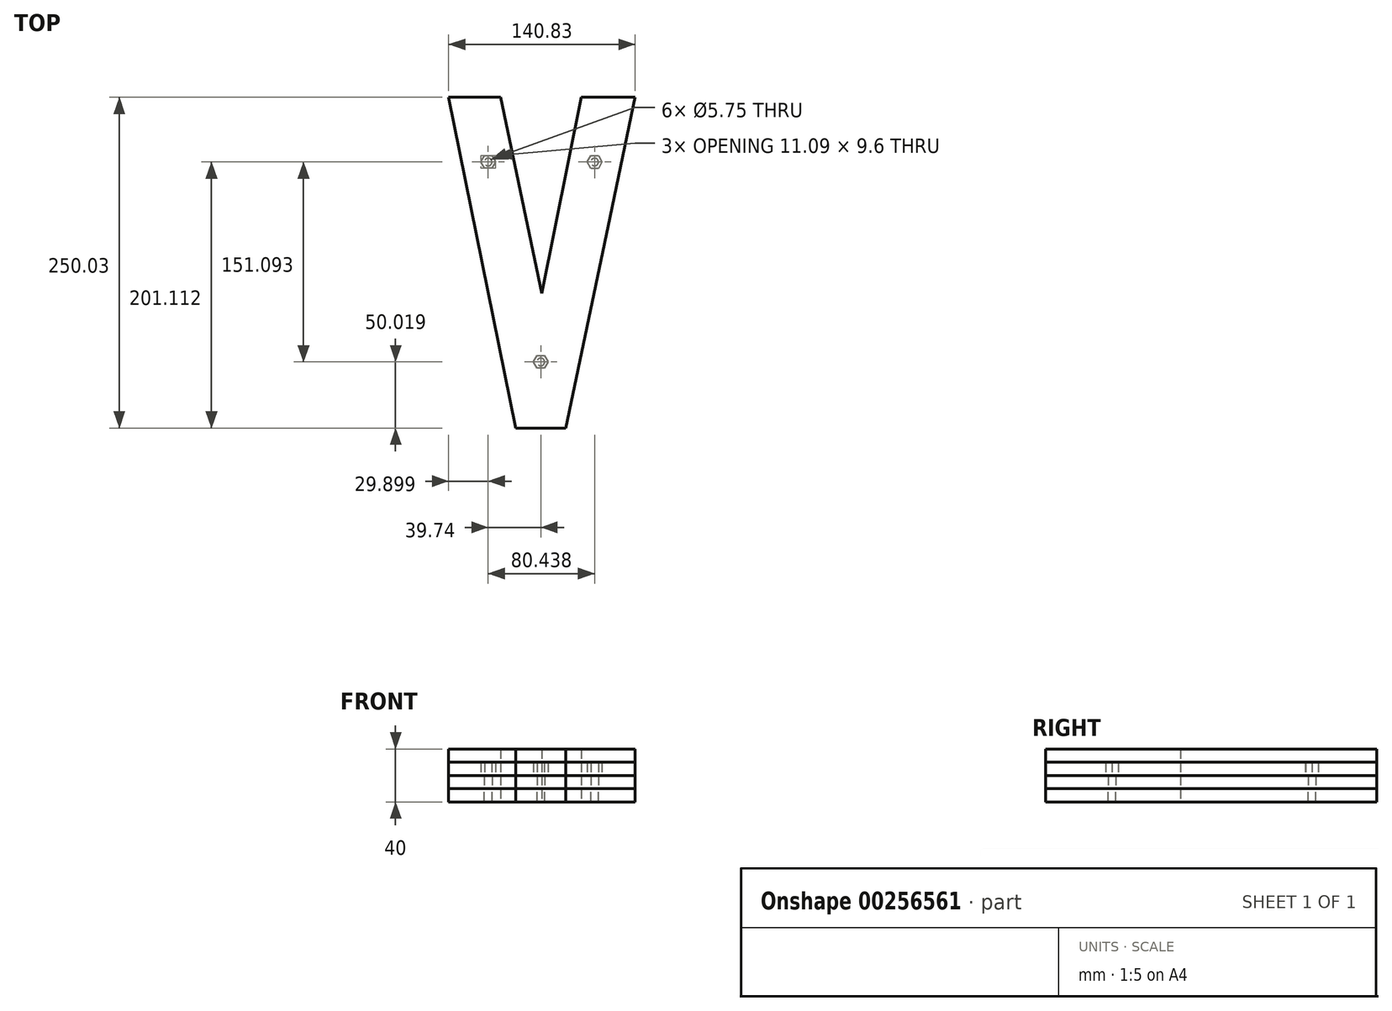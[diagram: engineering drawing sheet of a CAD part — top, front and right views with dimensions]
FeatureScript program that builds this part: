
annotation { "Feature Type Name" : "Feature", "Feature Type Description" : "" }
export const myFeature = defineFeature(function(context is Context, id is Id, definition is map)
    precondition{}
    {
        {
            assignVariable(context, id + "F0", {"name" : "spessore_materiale", "anyValue" : 10 * mm});
        }
        {
            var Q0;
            Q0=qCreatedBy(makeId("Top.planeOp"),FACE);
            var sketch = newSketch(context, id + "F1", { "sketchPlane" : qUnion([Q0])});
            skLineSegment(sketch, "E0", {"start": v(35.05, -81.42) * mm, "end": v(-32.7, -81.42) * mm});
            skLineSegment(sketch, "E1", {"start": v(-32.7, -81.42) * mm, "end": v(-112.73, 81.45) * mm});
            skLineSegment(sketch, "E2", {"start": v(-112.73, 81.45) * mm, "end": v(-56.97, 81.45) * mm});
            skLineSegment(sketch, "E3", {"start": v(-56.97, 81.45) * mm, "end": v(-0.74, -33) * mm});
            skLineSegment(sketch, "E4", {"start": v(-0.74, -33) * mm, "end": v(100.6, 204.64) * mm});
            skLineSegment(sketch, "E5", {"start": v(100.6, 204.64) * mm, "end": v(109.53, 225.59) * mm});
            skFitSpline(sketch, "E6", {"points": [v(109.53, 225.59) * mm, v(101.4, 226.06) * mm, v(93.16, 226.36) * mm, v(84.86, 226.36) * mm]});
            skFitSpline(sketch, "E7", {"points": [v(84.86, 226.36) * mm, v(83.84, 226.36) * mm, v(82.9, 226.32) * mm, v(81.9, 226.3) * mm]});
            skFitSpline(sketch, "E8", {"points": [v(81.9, 226.3) * mm, v(-87.62, 225.12) * mm, v(-225.03, 124.1) * mm, v(-225.03, 0) * mm]});
            skFitSpline(sketch, "E9", {"points": [v(-225.03, 0) * mm, v(-225.03, -111.84) * mm, v(-113.38, -204.88) * mm, v(32.74, -223.05) * mm]});
            skLineSegment(sketch, "E10", {"start": v(32.74, -223.05) * mm, "end": v(41.46, -202.6) * mm});
            skFitSpline(sketch, "E11", {"points": [v(41.46, -202.6) * mm, v(-97.09, -187.68) * mm, v(-203.61, -102.5) * mm, v(-203.61, 0) * mm]});
            skFitSpline(sketch, "E12", {"points": [v(-203.61, 0) * mm, v(-203.61, 110.11) * mm, v(-80.73, 200.17) * mm, v(72.69, 204.72) * mm]});
            skLineSegment(sketch, "E13", {"start": v(72.69, 204.72) * mm, "end": v(-2.4, 28.63) * mm});
            skLineSegment(sketch, "E14", {"start": v(-2.4, 28.63) * mm, "end": v(-40.98, 107.15) * mm});
            skLineSegment(sketch, "E15", {"start": v(-40.98, 107.15) * mm, "end": v(-153.98, 107.15) * mm});
            skLineSegment(sketch, "E16", {"start": v(-153.98, 107.15) * mm, "end": v(-54.89, -94.58) * mm});
            skLineSegment(sketch, "E17", {"start": v(-54.89, -94.58) * mm, "end": v(-60.1, -107.14) * mm});
            skLineSegment(sketch, "E18", {"start": v(-60.1, -107.14) * mm, "end": v(43.68, -107.14) * mm});
            skLineSegment(sketch, "E19", {"start": v(43.68, -107.14) * mm, "end": v(54.3, -107.06) * mm});
            skLineSegment(sketch, "E20", {"start": v(54.3, -107.06) * mm, "end": v(59, -96.15) * mm});
            skLineSegment(sketch, "E21", {"start": v(59, -96.15) * mm, "end": v(98.52, -3.43) * mm});
            skLineSegment(sketch, "E22", {"start": v(98.52, -3.43) * mm, "end": v(68.3, -3.43) * mm});
            skLineSegment(sketch, "E23", {"start": v(68.3, -3.43) * mm, "end": v(35.05, -81.42) * mm});
            skLineSegment(sketch, "E24", {"start": v(137.86, 222.98) * mm, "end": v(129.12, 202.52) * mm});
            skFitSpline(sketch, "E25", {"points": [v(129.12, 202.52) * mm, v(267.28, 187.34) * mm, v(373.37, 102.32) * mm, v(373.37, 0) * mm]});
            skFitSpline(sketch, "E26", {"points": [v(373.37, 0) * mm, v(373.37, -110.1) * mm, v(250.5, -200.17) * mm, v(97.07, -204.72) * mm]});
            skLineSegment(sketch, "E27", {"start": v(97.07, -204.72) * mm, "end": v(172.15, -28.63) * mm});
            skLineSegment(sketch, "E28", {"start": v(172.15, -28.63) * mm, "end": v(210.78, -107.14) * mm});
            skLineSegment(sketch, "E29", {"start": v(210.78, -107.14) * mm, "end": v(323.78, -107.14) * mm});
            skLineSegment(sketch, "E30", {"start": v(323.78, -107.14) * mm, "end": v(224.66, 94.57) * mm});
            skLineSegment(sketch, "E31", {"start": v(224.66, 94.57) * mm, "end": v(229.86, 107.15) * mm});
            skLineSegment(sketch, "E32", {"start": v(229.86, 107.15) * mm, "end": v(126.1, 107.15) * mm});
            skLineSegment(sketch, "E33", {"start": v(126.1, 107.15) * mm, "end": v(115.42, 107.07) * mm});
            skLineSegment(sketch, "E34", {"start": v(115.42, 107.07) * mm, "end": v(110.77, 96.15) * mm});
            skLineSegment(sketch, "E35", {"start": v(110.77, 96.15) * mm, "end": v(68.3, -3.43) * mm});
            skLineSegment(sketch, "E36", {"start": v(68.3, -3.43) * mm, "end": v(98.52, -3.43) * mm});
            skLineSegment(sketch, "E37", {"start": v(98.52, -3.43) * mm, "end": v(134.69, 81.45) * mm});
            skLineSegment(sketch, "E38", {"start": v(134.69, 81.45) * mm, "end": v(202.47, 81.45) * mm});
            skLineSegment(sketch, "E39", {"start": v(202.47, 81.45) * mm, "end": v(282.51, -81.42) * mm});
            skLineSegment(sketch, "E40", {"start": v(282.51, -81.42) * mm, "end": v(226.76, -81.42) * mm});
            skLineSegment(sketch, "E41", {"start": v(226.76, -81.42) * mm, "end": v(170.53, 33) * mm});
            skLineSegment(sketch, "E42", {"start": v(170.53, 33) * mm, "end": v(69.16, -204.63) * mm});
            skLineSegment(sketch, "E43", {"start": v(69.16, -204.63) * mm, "end": v(60.26, -225.59) * mm});
            skFitSpline(sketch, "E44", {"points": [v(60.26, -225.59) * mm, v(68.36, -226.07) * mm, v(76.57, -226.36) * mm, v(84.86, -226.36) * mm]});
            skFitSpline(sketch, "E45", {"points": [v(84.86, -226.36) * mm, v(85.9, -226.36) * mm, v(86.86, -226.32) * mm, v(87.87, -226.32) * mm]});
            skFitSpline(sketch, "E46", {"points": [v(87.87, -226.32) * mm, v(257.36, -225.13) * mm, v(394.8, -124.08) * mm, v(394.8, 0) * mm]});
            skFitSpline(sketch, "E47", {"points": [v(394.8, 0) * mm, v(394.8, 111.62) * mm, v(283.58, 204.54) * mm, v(137.86, 222.98) * mm]});
            skFitSpline(sketch, "E48", {"points": [v(-624, 127.8) * mm, v(-635.1, 127.8) * mm, v(-645.9, 124.08) * mm, v(-654.8, 117.24) * mm]});
            skFitSpline(sketch, "E49", {"points": [v(-654.8, 117.24) * mm, v(-663.7, 124.08) * mm, v(-674.5, 127.8) * mm, v(-685.62, 127.8) * mm]});
            skFitSpline(sketch, "E50", {"points": [v(-685.62, 127.8) * mm, v(-713.74, 127.8) * mm, v(-736.62, 104.92) * mm, v(-736.62, 76.78) * mm]});
            skLineSegment(sketch, "E51", {"start": v(-736.62, 76.78) * mm, "end": v(-736.62, -123.73) * mm});
            skLineSegment(sketch, "E52", {"start": v(-736.62, -123.73) * mm, "end": v(-696.19, -123.73) * mm});
            skLineSegment(sketch, "E53", {"start": v(-696.19, -123.73) * mm, "end": v(-696.19, 76.78) * mm});
            skFitSpline(sketch, "E54", {"points": [v(-696.19, 76.78) * mm, v(-696.19, 82.6) * mm, v(-691.43, 87.35) * mm, v(-685.62, 87.35) * mm]});
            skFitSpline(sketch, "E55", {"points": [v(-685.62, 87.35) * mm, v(-679.76, 87.35) * mm, v(-675.03, 82.6) * mm, v(-675.03, 76.78) * mm]});
            skLineSegment(sketch, "E56", {"start": v(-675.03, 76.78) * mm, "end": v(-675.03, -123.73) * mm});
            skLineSegment(sketch, "E57", {"start": v(-675.03, -123.73) * mm, "end": v(-634.58, -123.73) * mm});
            skLineSegment(sketch, "E58", {"start": v(-634.58, -123.73) * mm, "end": v(-634.58, 76.78) * mm});
            skFitSpline(sketch, "E59", {"points": [v(-634.58, 76.78) * mm, v(-634.58, 82.6) * mm, v(-629.83, 87.35) * mm, v(-624, 87.35) * mm]});
            skFitSpline(sketch, "E60", {"points": [v(-624, 87.35) * mm, v(-618.16, 87.35) * mm, v(-613.4, 82.6) * mm, v(-613.4, 76.78) * mm]});
            skLineSegment(sketch, "E61", {"start": v(-613.4, 76.78) * mm, "end": v(-613.4, -123.73) * mm});
            skLineSegment(sketch, "E62", {"start": v(-613.4, -123.73) * mm, "end": v(-572.97, -123.73) * mm});
            skLineSegment(sketch, "E63", {"start": v(-572.97, -123.73) * mm, "end": v(-572.97, 76.78) * mm});
            skFitSpline(sketch, "E64", {"points": [v(-572.97, 76.78) * mm, v(-572.97, 104.92) * mm, v(-595.85, 127.8) * mm, v(-624, 127.8) * mm]});
            skLineSegment(sketch, "E65", {"start": v(-331.84, -21.2) * mm, "end": v(-364.08, -21.2) * mm});
            skLineSegment(sketch, "E66", {"start": v(-364.08, -21.2) * mm, "end": v(-364.08, 69.71) * mm});
            skFitSpline(sketch, "E67", {"points": [v(-364.08, 69.71) * mm, v(-364.08, 78.61) * mm, v(-356.86, 85.84) * mm, v(-347.97, 85.84) * mm]});
            skFitSpline(sketch, "E68", {"points": [v(-347.97, 85.84) * mm, v(-339.08, 85.84) * mm, v(-331.84, 78.61) * mm, v(-331.84, 69.71) * mm]});
            skLineSegment(sketch, "E69", {"start": v(-331.84, 69.71) * mm, "end": v(-331.84, -21.2) * mm});
            skLineSegment(sketch, "E70", {"start": v(-291.4, -21.2) * mm, "end": v(-291.4, 69.71) * mm});
            skFitSpline(sketch, "E71", {"points": [v(-291.4, 69.71) * mm, v(-291.4, 100.9) * mm, v(-316.78, 126.28) * mm, v(-347.97, 126.28) * mm]});
            skFitSpline(sketch, "E72", {"points": [v(-347.97, 126.28) * mm, v(-379.15, 126.28) * mm, v(-404.53, 100.9) * mm, v(-404.53, 69.71) * mm]});
            skLineSegment(sketch, "E73", {"start": v(-404.53, 69.71) * mm, "end": v(-404.53, -21.2) * mm});
            skLineSegment(sketch, "E74", {"start": v(-404.53, -21.2) * mm, "end": v(-419.68, -21.2) * mm});
            skLineSegment(sketch, "E75", {"start": v(-419.68, -21.2) * mm, "end": v(-419.68, -61.63) * mm});
            skLineSegment(sketch, "E76", {"start": v(-419.68, -61.63) * mm, "end": v(-404.53, -61.63) * mm});
            skLineSegment(sketch, "E77", {"start": v(-404.53, -61.63) * mm, "end": v(-404.53, -124.49) * mm});
            skLineSegment(sketch, "E78", {"start": v(-404.53, -124.49) * mm, "end": v(-364.08, -124.49) * mm});
            skLineSegment(sketch, "E79", {"start": v(-364.08, -124.49) * mm, "end": v(-364.08, -61.63) * mm});
            skLineSegment(sketch, "E80", {"start": v(-364.08, -61.63) * mm, "end": v(-331.84, -61.63) * mm});
            skLineSegment(sketch, "E81", {"start": v(-331.84, -61.63) * mm, "end": v(-331.84, -124.49) * mm});
            skLineSegment(sketch, "E82", {"start": v(-331.84, -124.49) * mm, "end": v(-291.4, -124.49) * mm});
            skLineSegment(sketch, "E83", {"start": v(-291.4, -124.49) * mm, "end": v(-291.4, -61.63) * mm});
            skLineSegment(sketch, "E84", {"start": v(-291.4, -61.63) * mm, "end": v(-276.26, -61.63) * mm});
            skLineSegment(sketch, "E85", {"start": v(-276.26, -61.63) * mm, "end": v(-276.26, -21.2) * mm});
            skLineSegment(sketch, "E86", {"start": v(-276.26, -21.2) * mm, "end": v(-291.4, -21.2) * mm});
            skLineSegment(sketch, "E87", {"start": v(-806.97, 50.95) * mm, "end": v(-806.97, 85.84) * mm});
            skLineSegment(sketch, "E88", {"start": v(-806.97, 85.84) * mm, "end": v(-754.28, 85.84) * mm});
            skLineSegment(sketch, "E89", {"start": v(-754.28, 85.84) * mm, "end": v(-754.28, 126.28) * mm});
            skLineSegment(sketch, "E90", {"start": v(-754.28, 126.28) * mm, "end": v(-847.4, 126.28) * mm});
            skLineSegment(sketch, "E91", {"start": v(-847.4, 126.28) * mm, "end": v(-847.4, 14.3) * mm});
            skLineSegment(sketch, "E92", {"start": v(-847.4, 14.3) * mm, "end": v(-867.4, 14.3) * mm});
            skLineSegment(sketch, "E93", {"start": v(-867.4, 14.3) * mm, "end": v(-867.4, -26.13) * mm});
            skLineSegment(sketch, "E94", {"start": v(-867.4, -26.13) * mm, "end": v(-847.4, -26.13) * mm});
            skLineSegment(sketch, "E95", {"start": v(-847.4, -26.13) * mm, "end": v(-847.4, -124.49) * mm});
            skLineSegment(sketch, "E96", {"start": v(-847.4, -124.49) * mm, "end": v(-754.28, -124.49) * mm});
            skLineSegment(sketch, "E97", {"start": v(-754.28, -124.49) * mm, "end": v(-754.28, -84.05) * mm});
            skLineSegment(sketch, "E98", {"start": v(-754.28, -84.05) * mm, "end": v(-806.97, -84.05) * mm});
            skLineSegment(sketch, "E99", {"start": v(-806.97, -84.05) * mm, "end": v(-806.97, -26.13) * mm});
            skLineSegment(sketch, "E100", {"start": v(-806.97, -26.13) * mm, "end": v(-761.6, -26.13) * mm});
            skLineSegment(sketch, "E101", {"start": v(-761.6, -26.13) * mm, "end": v(-761.6, 14.3) * mm});
            skLineSegment(sketch, "E102", {"start": v(-761.6, 14.3) * mm, "end": v(-806.97, 14.3) * mm});
            skLineSegment(sketch, "E103", {"start": v(-806.97, 14.3) * mm, "end": v(-806.97, 50.95) * mm});
            skLineSegment(sketch, "E104", {"start": v(-909.64, 126.28) * mm, "end": v(-912.48, 126.28) * mm});
            skLineSegment(sketch, "E105", {"start": v(-912.48, 126.28) * mm, "end": v(-942.35, -21.84) * mm});
            skLineSegment(sketch, "E106", {"start": v(-942.35, -21.84) * mm, "end": v(-973.61, 126.28) * mm});
            skLineSegment(sketch, "E107", {"start": v(-973.61, 126.28) * mm, "end": v(-1012.76, 126.28) * mm});
            skLineSegment(sketch, "E108", {"start": v(-1012.76, 126.28) * mm, "end": v(-962.19, -123.72) * mm});
            skLineSegment(sketch, "E109", {"start": v(-962.19, -123.72) * mm, "end": v(-924.13, -123.75) * mm});
            skLineSegment(sketch, "E110", {"start": v(-924.13, -123.75) * mm, "end": v(-892.27, 28.86) * mm});
            skLineSegment(sketch, "E111", {"start": v(-892.27, 28.86) * mm, "end": v(-871.93, 126.28) * mm});
            skLineSegment(sketch, "E112", {"start": v(-871.93, 126.28) * mm, "end": v(-909.64, 126.28) * mm});
            skFitSpline(sketch, "E113", {"points": [v(-467.48, 32.6) * mm, v(-467.83, 28.64) * mm, v(-468.5, 24.7) * mm, v(-469.6, 20.88) * mm]});
            skFitSpline(sketch, "E114", {"points": [v(-469.6, 20.88) * mm, v(-470.64, 17.24) * mm, v(-472.02, 13.7) * mm, v(-473.8, 10.38) * mm]});
            skFitSpline(sketch, "E115", {"points": [v(-473.8, 10.38) * mm, v(-476.8, 4.87) * mm, v(-481.2, -0.04) * mm, v(-486.15, -3.83) * mm]});
            skFitSpline(sketch, "E116", {"points": [v(-486.15, -3.83) * mm, v(-488.25, -5.43) * mm, v(-490.48, -6.91) * mm, v(-492.77, -8.22) * mm]});
            skFitSpline(sketch, "E117", {"points": [v(-492.77, -8.22) * mm, v(-492.86, -8.25) * mm, v(-493.01, -8.33) * mm, v(-493.22, -8.42) * mm]});
            skLineSegment(sketch, "E118", {"start": v(-493.22, -8.42) * mm, "end": v(-499.47, -10.82) * mm});
            skLineSegment(sketch, "E119", {"start": v(-499.47, -10.82) * mm, "end": v(-499.47, -7.15) * mm});
            skLineSegment(sketch, "E120", {"start": v(-499.47, -7.15) * mm, "end": v(-499.47, 82.05) * mm});
            skFitSpline(sketch, "E121", {"points": [v(-499.47, 82.05) * mm, v(-488.07, 80.86) * mm, v(-475.47, 71.05) * mm, v(-470.67, 59.15) * mm]});
            skFitSpline(sketch, "E122", {"points": [v(-470.67, 59.15) * mm, v(-467.23, 50.68) * mm, v(-466.7, 41.63) * mm, v(-467.48, 32.6) * mm]});
            skFitSpline(sketch, "E123", {"points": [v(-426.58, 47.71) * mm, v(-427.42, 57.64) * mm, v(-429.87, 67.46) * mm, v(-433.61, 76.7) * mm]});
            skFitSpline(sketch, "E124", {"points": [v(-433.61, 76.7) * mm, v(-445.03, 104.92) * mm, v(-473.34, 125.66) * mm, v(-500.92, 126.06) * mm]});
            skFitSpline(sketch, "E125", {"points": [v(-500.92, 126.06) * mm, v(-502.53, 126.08) * mm, v(-504.16, 126.08) * mm, v(-505.77, 126.1) * mm]});
            skFitSpline(sketch, "E126", {"points": [v(-505.77, 126.1) * mm, v(-505.77, 126.15) * mm, v(-505.8, 126.2) * mm, v(-505.8, 126.26) * mm]});
            skLineSegment(sketch, "E127", {"start": v(-505.8, 126.26) * mm, "end": v(-521.5, 126.24) * mm});
            skFitSpline(sketch, "E128", {"points": [v(-515.14, 126.24) * mm, v(-515.15, 126.26) * mm, v(-515.18, 126.26) * mm, v(-515.18, 126.28) * mm]});
            skLineSegment(sketch, "E129", {"start": v(-521.5, 126.24) * mm, "end": v(-539.9, 126.23) * mm});
            skLineSegment(sketch, "E130", {"start": v(-539.9, 126.23) * mm, "end": v(-539.9, -16.92) * mm});
            skFitSpline(sketch, "E131", {"points": [v(-539.9, -16.92) * mm, v(-542.63, -17.07) * mm, v(-545.34, -17.16) * mm, v(-548.01, -17.2) * mm]});
            skLineSegment(sketch, "E132", {"start": v(-548.01, -17.2) * mm, "end": v(-553.01, -17.32) * mm});
            skLineSegment(sketch, "E133", {"start": v(-553.01, -17.32) * mm, "end": v(-553.01, -57.74) * mm});
            skFitSpline(sketch, "E134", {"points": [v(-547.8, -57.63) * mm, v(-545.18, -57.61) * mm, v(-542.54, -57.56) * mm, v(-539.9, -57.5) * mm]});
            skLineSegment(sketch, "E135", {"start": v(-539.9, -57.5) * mm, "end": v(-539.9, -124.49) * mm});
            skLineSegment(sketch, "E136", {"start": v(-539.9, -124.49) * mm, "end": v(-499.47, -124.49) * mm});
            skLineSegment(sketch, "E137", {"start": v(-499.47, -124.49) * mm, "end": v(-499.47, -54.72) * mm});
            skFitSpline(sketch, "E138", {"points": [v(-499.47, -54.72) * mm, v(-494.31, -53.36) * mm, v(-489.31, -51.43) * mm, v(-484.7, -49.05) * mm]});
            skFitSpline(sketch, "E139", {"points": [v(-484.7, -49.05) * mm, v(-467.71, -40.29) * mm, v(-452.27, -26.51) * mm, v(-441.84, -10.46) * mm]});
            skFitSpline(sketch, "E140", {"points": [v(-441.84, -10.46) * mm, v(-438.88, -5.92) * mm, v(-436.16, -1.02) * mm, v(-434.04, 3.97) * mm]});
            skFitSpline(sketch, "E141", {"points": [v(-434.04, 3.97) * mm, v(-429.58, 14.49) * mm, v(-426.66, 25.76) * mm, v(-426.32, 37.22) * mm]});
            skFitSpline(sketch, "E142", {"points": [v(-426.32, 37.22) * mm, v(-426.19, 40.73) * mm, v(-426.28, 44.22) * mm, v(-426.58, 47.71) * mm]});
            skLineSegment(sketch, "E143", {"start": v(537.35, -29.05) * mm, "end": v(505.12, -29.05) * mm});
            skLineSegment(sketch, "E144", {"start": v(505.12, -29.05) * mm, "end": v(505.12, 61.86) * mm});
            skFitSpline(sketch, "E145", {"points": [v(505.12, 61.86) * mm, v(505.12, 70.76) * mm, v(512.33, 78) * mm, v(521.2, 78) * mm]});
            skFitSpline(sketch, "E146", {"points": [v(521.2, 78) * mm, v(530.14, 78) * mm, v(537.35, 70.76) * mm, v(537.35, 61.86) * mm]});
            skLineSegment(sketch, "E147", {"start": v(537.35, 61.86) * mm, "end": v(537.35, -29.05) * mm});
            skLineSegment(sketch, "E148", {"start": v(577.78, -7.93) * mm, "end": v(577.78, 61.86) * mm});
            skFitSpline(sketch, "E149", {"points": [v(577.78, 61.86) * mm, v(577.78, 93.05) * mm, v(552.38, 118.42) * mm, v(521.2, 118.42) * mm]});
            skFitSpline(sketch, "E150", {"points": [v(521.2, 118.42) * mm, v(490.03, 118.42) * mm, v(464.64, 93.05) * mm, v(464.64, 61.86) * mm]});
            skLineSegment(sketch, "E151", {"start": v(464.64, 61.86) * mm, "end": v(464.64, -29.05) * mm});
            skLineSegment(sketch, "E152", {"start": v(464.64, -29.05) * mm, "end": v(449.5, -29.05) * mm});
            skLineSegment(sketch, "E153", {"start": v(449.5, -29.05) * mm, "end": v(449.5, -69.48) * mm});
            skLineSegment(sketch, "E154", {"start": v(449.5, -69.48) * mm, "end": v(464.64, -69.48) * mm});
            skLineSegment(sketch, "E155", {"start": v(464.64, -69.48) * mm, "end": v(464.64, -132.33) * mm});
            skLineSegment(sketch, "E156", {"start": v(464.64, -132.33) * mm, "end": v(505.12, -132.33) * mm});
            skLineSegment(sketch, "E157", {"start": v(505.12, -132.33) * mm, "end": v(505.12, -69.48) * mm});
            skLineSegment(sketch, "E158", {"start": v(505.12, -69.48) * mm, "end": v(537.35, -69.48) * mm});
            skLineSegment(sketch, "E159", {"start": v(537.35, -69.48) * mm, "end": v(537.35, -132.33) * mm});
            skLineSegment(sketch, "E160", {"start": v(537.35, -132.33) * mm, "end": v(577.78, -132.33) * mm});
            skLineSegment(sketch, "E161", {"start": v(577.78, -132.33) * mm, "end": v(577.78, -69.48) * mm});
            skLineSegment(sketch, "E162", {"start": v(577.78, -69.48) * mm, "end": v(592.93, -69.48) * mm});
            skLineSegment(sketch, "E163", {"start": v(592.93, -69.48) * mm, "end": v(592.93, -29.05) * mm});
            skLineSegment(sketch, "E164", {"start": v(592.93, -29.05) * mm, "end": v(577.78, -29.05) * mm});
            skLineSegment(sketch, "E165", {"start": v(577.78, -29.05) * mm, "end": v(577.78, -7.93) * mm});
            skLineSegment(sketch, "E166", {"start": v(690.45, 22.21) * mm, "end": v(690.45, -75.78) * mm});
            skFitSpline(sketch, "E167", {"points": [v(690.45, -75.78) * mm, v(690.45, -84.66) * mm, v(683.2, -91.9) * mm, v(674.32, -91.9) * mm]});
            skFitSpline(sketch, "E168", {"points": [v(674.32, -91.9) * mm, v(665.4, -91.9) * mm, v(658.2, -84.66) * mm, v(658.2, -75.78) * mm]});
            skLineSegment(sketch, "E169", {"start": v(658.2, -75.78) * mm, "end": v(658.2, 118.42) * mm});
            skLineSegment(sketch, "E170", {"start": v(658.2, 118.42) * mm, "end": v(617.77, 118.42) * mm});
            skLineSegment(sketch, "E171", {"start": v(617.77, 118.42) * mm, "end": v(617.77, -75.78) * mm});
            skFitSpline(sketch, "E172", {"points": [v(617.77, -75.78) * mm, v(617.77, -106.96) * mm, v(643.15, -132.33) * mm, v(674.32, -132.33) * mm]});
            skFitSpline(sketch, "E173", {"points": [v(674.32, -132.33) * mm, v(705.48, -132.33) * mm, v(730.88, -106.96) * mm, v(730.88, -75.78) * mm]});
            skLineSegment(sketch, "E174", {"start": v(730.88, -75.78) * mm, "end": v(730.88, 118.42) * mm});
            skLineSegment(sketch, "E175", {"start": v(730.88, 118.42) * mm, "end": v(690.45, 118.42) * mm});
            skLineSegment(sketch, "E176", {"start": v(690.45, 118.42) * mm, "end": v(690.45, 22.21) * mm});
            skLineSegment(sketch, "E177", {"start": v(972.32, -26.98) * mm, "end": v(972.32, -75.78) * mm});
            skFitSpline(sketch, "E178", {"points": [v(972.32, -75.78) * mm, v(972.32, -84.66) * mm, v(965.1, -91.9) * mm, v(956.18, -91.9) * mm]});
            skFitSpline(sketch, "E179", {"points": [v(956.18, -91.9) * mm, v(947.29, -91.9) * mm, v(940.08, -84.66) * mm, v(940.08, -75.78) * mm]});
            skLineSegment(sketch, "E180", {"start": v(940.08, -75.78) * mm, "end": v(940.08, 61.86) * mm});
            skFitSpline(sketch, "E181", {"points": [v(940.08, 61.86) * mm, v(940.08, 70.76) * mm, v(947.29, 78) * mm, v(956.18, 78) * mm]});
            skFitSpline(sketch, "E182", {"points": [v(956.18, 78) * mm, v(965.1, 78) * mm, v(972.32, 70.76) * mm, v(972.32, 61.86) * mm]});
            skLineSegment(sketch, "E183", {"start": v(972.32, 61.86) * mm, "end": v(972.32, -26.98) * mm});
            skFitSpline(sketch, "E184", {"points": [v(956.18, 118.42) * mm, v(925.02, 118.42) * mm, v(899.63, 93.05) * mm, v(899.63, 61.86) * mm]});
            skLineSegment(sketch, "E185", {"start": v(899.63, 61.86) * mm, "end": v(899.63, -75.78) * mm});
            skFitSpline(sketch, "E186", {"points": [v(899.63, -75.78) * mm, v(899.63, -106.96) * mm, v(925.02, -132.33) * mm, v(956.18, -132.33) * mm]});
            skFitSpline(sketch, "E187", {"points": [v(956.18, -132.33) * mm, v(987.38, -132.33) * mm, v(1012.76, -106.96) * mm, v(1012.76, -75.78) * mm]});
            skLineSegment(sketch, "E188", {"start": v(1012.76, -75.78) * mm, "end": v(1012.76, 61.86) * mm});
            skFitSpline(sketch, "E189", {"points": [v(1012.76, 61.86) * mm, v(1012.76, 93.05) * mm, v(987.38, 118.42) * mm, v(956.18, 118.42) * mm]});
            skLineSegment(sketch, "E190", {"start": v(753.34, 78) * mm, "end": v(796, 78) * mm});
            skLineSegment(sketch, "E191", {"start": v(796, 78) * mm, "end": v(796, -132.33) * mm});
            skLineSegment(sketch, "E192", {"start": v(796, -132.33) * mm, "end": v(836.48, -132.33) * mm});
            skLineSegment(sketch, "E193", {"start": v(836.48, -132.33) * mm, "end": v(836.48, 78) * mm});
            skLineSegment(sketch, "E194", {"start": v(836.48, 78) * mm, "end": v(879.09, 78) * mm});
            skLineSegment(sketch, "E195", {"start": v(879.09, 78) * mm, "end": v(879.09, 118.42) * mm});
            skLineSegment(sketch, "E196", {"start": v(879.09, 118.42) * mm, "end": v(753.34, 118.42) * mm});
            skLineSegment(sketch, "E197", {"start": v(753.34, 118.42) * mm, "end": v(753.34, 78) * mm});
            skLineSegment(sketch, "E198", {"start": v(-547.8, -57.63) * mm, "end": v(-553.01, -57.74) * mm});
            skSolve(sketch);
        }
        {
            var Q0;
            Q0=makeQuery(id+"F1.imprint","IMPRINT",FACE,{"disambiguationData":[TD([[makeQuery(id+"F1.imprint","IMPRINT",EDGE,{"derivedFrom":sQuery(id+"F1.wireOp",EDGE,"E104")}),1.0]])]});
            var Q1;
            Q1=makeQuery(id+"F1.imprint","IMPRINT",FACE,{"disambiguationData":[TD([[makeQuery(id+"F1.imprint","IMPRINT",EDGE,{"derivedFrom":sQuery(id+"F1.wireOp",EDGE,"E87")}),1.0]])]});
            var Q2;
            Q2=makeQuery(id+"F1.imprint","IMPRINT",FACE,{"disambiguationData":[TD([[makeQuery(id+"F1.imprint","IMPRINT",EDGE,{"derivedFrom":sQuery(id+"F1.wireOp",EDGE,"E48")}),1.0]])]});
            var Q3;
            Q3=makeQuery(id+"F1.imprint","IMPRINT",FACE,{"disambiguationData":[TD([[makeQuery(id+"F1.imprint","IMPRINT",EDGE,{"derivedFrom":sQuery(id+"F1.wireOp",EDGE,"E113")}),1.0]])]});
            var Q4;
            Q4=makeQuery(id+"F1.imprint","IMPRINT",FACE,{"disambiguationData":[TD([[makeQuery(id+"F1.imprint","IMPRINT",EDGE,{"derivedFrom":sQuery(id+"F1.wireOp",EDGE,"E65")}),1.0]])]});
            var Q5;
            Q5=makeQuery(id+"F1.imprint","IMPRINT",FACE,{"disambiguationData":[TD([[makeQuery(id+"F1.imprint","IMPRINT",EDGE,{"derivedFrom":sQuery(id+"F1.wireOp",EDGE,"E0")}),1.0]])]});
            extrude(context, id + "F2", {"entities" : qUnion([Q0, Q1, Q2, Q3, Q4, Q5]), "depth" : getVariable(context, 'spessore_materiale')});
        }
        {
            var Q0;
            Q0=makeQuery(id+"F1.imprint","IMPRINT",FACE,{"disambiguationData":[TD([[makeQuery(id+"F1.imprint","IMPRINT",EDGE,{"derivedFrom":sQuery(id+"F1.wireOp",EDGE,"E24")}),1.0]])]});
            var Q1;
            Q1=makeQuery(id+"F1.imprint","IMPRINT",FACE,{"disambiguationData":[TD([[makeQuery(id+"F1.imprint","IMPRINT",EDGE,{"derivedFrom":sQuery(id+"F1.wireOp",EDGE,"E143")}),1.0]])]});
            var Q2;
            Q2=makeQuery(id+"F1.imprint","IMPRINT",FACE,{"disambiguationData":[TD([[makeQuery(id+"F1.imprint","IMPRINT",EDGE,{"derivedFrom":sQuery(id+"F1.wireOp",EDGE,"E166")}),1.0]])]});
            var Q3;
            Q3=makeQuery(id+"F1.imprint","IMPRINT",FACE,{"disambiguationData":[TD([[makeQuery(id+"F1.imprint","IMPRINT",EDGE,{"derivedFrom":sQuery(id+"F1.wireOp",EDGE,"E190")}),1.0]])]});
            var Q4;
            Q4=makeQuery(id+"F1.imprint","IMPRINT",FACE,{"disambiguationData":[TD([[makeQuery(id+"F1.imprint","IMPRINT",EDGE,{"derivedFrom":sQuery(id+"F1.wireOp",EDGE,"E177")}),1.0]])]});
            extrude(context, id + "F3", {"entities" : qUnion([Q0, Q1, Q2, Q3, Q4]), "depth" : getVariable(context, 'spessore_materiale')});
        }
        {
            var Q0;
            Q0=makeQuery(id+"F2.opExtrude","CAP_FACE",FACE,{"disambiguationData":[OSD([sQuery(id+"F1.wireOp",EDGE,"E104"),sQuery(id+"F1.wireOp",EDGE,"E105"),sQuery(id+"F1.wireOp",EDGE,"E106"),sQuery(id+"F1.wireOp",EDGE,"E107"),sQuery(id+"F1.wireOp",EDGE,"E108"),sQuery(id+"F1.wireOp",EDGE,"E109"),sQuery(id+"F1.wireOp",EDGE,"E110"),sQuery(id+"F1.wireOp",EDGE,"E111"),sQuery(id+"F1.wireOp",EDGE,"E112")])],"isStart":false});
            var sketch = newSketch(context, id + "F4", { "sketchPlane" : qUnion([Q0])});
            skLineSegment(sketch, "E199", {"start": v(-973.61, 126.28) * mm, "end": v(-942.35, -21.84) * mm, "construction": true});
            skLineSegment(sketch, "E200", {"start": v(-942.35, -21.84) * mm, "end": v(-912.48, 126.28) * mm, "construction": true});
            skLineSegment(sketch, "E201", {"start": v(-993.19, 126.28) * mm, "end": v(-982.86, 77.36) * mm, "construction": true});
            skLineSegment(sketch, "E202", {"start": v(-892.2, 126.28) * mm, "end": v(-902.42, 77.34) * mm, "construction": true});
            skLineSegment(sketch, "E203", {"start": v(-943.16, -123.73) * mm, "end": v(-943.12, -73.73) * mm, "construction": true});
            skCircle(sketch, "E204", {"center": v(-982.86, 77.36) * mm, "radius": 2.88 * mm});
            skCircle(sketch, "E205", {"center": v(-902.42, 77.34) * mm, "radius": 2.88 * mm});
            skCircle(sketch, "E206", {"center": v(-943.12, -73.73) * mm, "radius": 2.88 * mm});
            skSolve(sketch);
        }
        {
            var Q0;
            Q0=makeQuery(id+"F4.imprint","IMPRINT",FACE,{"disambiguationData":[TD([[makeQuery(id+"F4.imprint","IMPRINT",EDGE,{"derivedFrom":sQuery(id+"F4.wireOp",EDGE,"E204")}),-1.0]])]});
            var Q1;
            Q1=makeQuery(id+"F2.opExtrude","CAP_FACE",FACE,{"disambiguationData":[OSD([sQuery(id+"F1.wireOp",EDGE,"E104"),sQuery(id+"F1.wireOp",EDGE,"E105"),sQuery(id+"F1.wireOp",EDGE,"E106"),sQuery(id+"F1.wireOp",EDGE,"E107"),sQuery(id+"F1.wireOp",EDGE,"E108"),sQuery(id+"F1.wireOp",EDGE,"E109"),sQuery(id+"F1.wireOp",EDGE,"E110"),sQuery(id+"F1.wireOp",EDGE,"E111"),sQuery(id+"F1.wireOp",EDGE,"E112")])],"isStart":true});
            extrude(context, id + "F5", {"entities" : qUnion([Q0]), "operationType" : NewBodyOperationType.INTERSECT, "endBound" : BoundingType.UP_TO_SURFACE, "oppositeDirection" : true, "endBoundEntityFace" : qUnion([Q1]), "depth" : getVariable(context, 'spessore_materiale')});
        }
        {
            var Q0;
            Q0=makeQuery(id+"F2.opExtrude","CAP_FACE",FACE,{"disambiguationData":[OSD([sQuery(id+"F1.wireOp",EDGE,"E104"),sQuery(id+"F1.wireOp",EDGE,"E105"),sQuery(id+"F1.wireOp",EDGE,"E106"),sQuery(id+"F1.wireOp",EDGE,"E107"),sQuery(id+"F1.wireOp",EDGE,"E108"),sQuery(id+"F1.wireOp",EDGE,"E109"),sQuery(id+"F1.wireOp",EDGE,"E110"),sQuery(id+"F1.wireOp",EDGE,"E111"),sQuery(id+"F1.wireOp",EDGE,"E112")])],"isStart":false});
            extrude(context, id + "F6", {"entities" : qUnion([Q0]), "depth" : getVariable(context, 'spessore_materiale')});
        }
        {
            var Q0;
            Q0=makeQuery(id+"F6.opExtrude","CAP_FACE",FACE,{"disambiguationData":[OSD([sQuery(id+"F1.wireOp",EDGE,"E104"),sQuery(id+"F1.wireOp",EDGE,"E105"),sQuery(id+"F1.wireOp",EDGE,"E106"),sQuery(id+"F1.wireOp",EDGE,"E107"),sQuery(id+"F1.wireOp",EDGE,"E108"),sQuery(id+"F1.wireOp",EDGE,"E109"),sQuery(id+"F1.wireOp",EDGE,"E110"),sQuery(id+"F1.wireOp",EDGE,"E111"),sQuery(id+"F1.wireOp",EDGE,"E112")])],"isStart":false});
            var sketch = newSketch(context, id + "F7", { "sketchPlane" : qUnion([Q0])});
            skLineSegment(sketch, "E207.0", {"start": v(-1012.76, 126.28) * mm, "end": v(-962.19, -123.72) * mm});
            skLineSegment(sketch, "E207.1", {"start": v(-973.61, 126.28) * mm, "end": v(-1012.76, 126.28) * mm});
            skLineSegment(sketch, "E207.2", {"start": v(-942.35, -21.84) * mm, "end": v(-973.61, 126.28) * mm});
            skLineSegment(sketch, "E207.3", {"start": v(-912.48, 126.28) * mm, "end": v(-942.35, -21.84) * mm});
            skLineSegment(sketch, "E207.4", {"start": v(-871.93, 126.28) * mm, "end": v(-912.48, 126.28) * mm});
            skLineSegment(sketch, "E207.5", {"start": v(-892.27, 28.86) * mm, "end": v(-871.93, 126.28) * mm});
            skLineSegment(sketch, "E207.6", {"start": v(-962.19, -123.72) * mm, "end": v(-924.13, -123.75) * mm});
            skLineSegment(sketch, "E207.7", {"start": v(-924.13, -123.75) * mm, "end": v(-892.27, 28.86) * mm});
            skCircle(sketch, "E208.cCircle", {"center": v(-982.86, 77.36) * mm, "radius": 4.8 * mm, "construction": true});
            skLineSegment(sketch, "E208.0", {"start": v(-977.32, 77.36) * mm, "end": v(-980.09, 72.56) * mm});
            skLineSegment(sketch, "E208.1", {"start": v(-980.09, 72.56) * mm, "end": v(-985.63, 72.56) * mm});
            skLineSegment(sketch, "E208.2", {"start": v(-985.63, 72.56) * mm, "end": v(-988.4, 77.36) * mm});
            skLineSegment(sketch, "E208.3", {"start": v(-988.4, 77.36) * mm, "end": v(-985.63, 82.16) * mm});
            skLineSegment(sketch, "E208.4", {"start": v(-985.63, 82.16) * mm, "end": v(-980.09, 82.16) * mm});
            skLineSegment(sketch, "E208.5", {"start": v(-980.09, 82.16) * mm, "end": v(-977.32, 77.36) * mm});
            skPoint(sketch, "E208.0.midPoint", {"position": v(-978.7, 74.96) * mm});
            skCircle(sketch, "E209.cCircle", {"center": v(-902.42, 77.34) * mm, "radius": 4.8 * mm, "construction": true});
            skLineSegment(sketch, "E209.0", {"start": v(-896.88, 77.34) * mm, "end": v(-899.65, 72.54) * mm});
            skLineSegment(sketch, "E209.1", {"start": v(-899.65, 72.54) * mm, "end": v(-905.2, 72.54) * mm});
            skLineSegment(sketch, "E209.2", {"start": v(-905.2, 72.54) * mm, "end": v(-907.97, 77.34) * mm});
            skLineSegment(sketch, "E209.3", {"start": v(-907.97, 77.34) * mm, "end": v(-905.2, 82.14) * mm});
            skLineSegment(sketch, "E209.4", {"start": v(-905.2, 82.14) * mm, "end": v(-899.65, 82.14) * mm});
            skLineSegment(sketch, "E209.5", {"start": v(-899.65, 82.14) * mm, "end": v(-896.88, 77.34) * mm});
            skPoint(sketch, "E209.0.midPoint", {"position": v(-898.27, 74.94) * mm});
            skCircle(sketch, "E210.cCircle", {"center": v(-943.12, -73.73) * mm, "radius": 4.8 * mm, "construction": true});
            skLineSegment(sketch, "E210.0", {"start": v(-937.58, -73.73) * mm, "end": v(-940.35, -78.53) * mm});
            skLineSegment(sketch, "E210.1", {"start": v(-940.35, -78.53) * mm, "end": v(-945.9, -78.53) * mm});
            skLineSegment(sketch, "E210.2", {"start": v(-945.9, -78.53) * mm, "end": v(-948.66, -73.73) * mm});
            skLineSegment(sketch, "E210.3", {"start": v(-948.66, -73.73) * mm, "end": v(-945.9, -68.93) * mm});
            skLineSegment(sketch, "E210.4", {"start": v(-945.9, -68.93) * mm, "end": v(-940.35, -68.93) * mm});
            skLineSegment(sketch, "E210.5", {"start": v(-940.35, -68.93) * mm, "end": v(-937.58, -73.73) * mm});
            skPoint(sketch, "E210.0.midPoint", {"position": v(-938.96, -76.13) * mm});
            skSolve(sketch);
        }
        {
            var Q0;
            Q0=makeQuery(id+"F7.imprint","IMPRINT",FACE,{"disambiguationData":[TD([[makeQuery(id+"F7.imprint","IMPRINT",EDGE,{"derivedFrom":sQuery(id+"F7.wireOp",EDGE,"E207.0")}),1.0]])]});
            extrude(context, id + "F8", {"entities" : qUnion([Q0]), "depth" : getVariable(context, 'spessore_materiale')});
        }
        {
            var Q0;
            Q0=makeQuery(id+"F8.opExtrude","CAP_FACE",FACE,{"disambiguationData":[OSD([sQuery(id+"F7.wireOp",EDGE,"E207.0"),sQuery(id+"F7.wireOp",EDGE,"E207.1"),sQuery(id+"F7.wireOp",EDGE,"E207.2"),sQuery(id+"F7.wireOp",EDGE,"E207.3"),sQuery(id+"F7.wireOp",EDGE,"E207.4"),sQuery(id+"F7.wireOp",EDGE,"E207.5"),sQuery(id+"F7.wireOp",EDGE,"E207.6"),sQuery(id+"F7.wireOp",EDGE,"E207.7"),sQuery(id+"F7.wireOp",EDGE,"E208.0"),sQuery(id+"F7.wireOp",EDGE,"E208.1"),sQuery(id+"F7.wireOp",EDGE,"E208.2"),sQuery(id+"F7.wireOp",EDGE,"E208.3"),sQuery(id+"F7.wireOp",EDGE,"E208.4"),sQuery(id+"F7.wireOp",EDGE,"E208.5"),sQuery(id+"F7.wireOp",EDGE,"E209.0"),sQuery(id+"F7.wireOp",EDGE,"E209.1"),sQuery(id+"F7.wireOp",EDGE,"E209.2"),sQuery(id+"F7.wireOp",EDGE,"E209.3"),sQuery(id+"F7.wireOp",EDGE,"E209.4"),sQuery(id+"F7.wireOp",EDGE,"E209.5"),sQuery(id+"F7.wireOp",EDGE,"E210.0"),sQuery(id+"F7.wireOp",EDGE,"E210.1"),sQuery(id+"F7.wireOp",EDGE,"E210.2"),sQuery(id+"F7.wireOp",EDGE,"E210.3"),sQuery(id+"F7.wireOp",EDGE,"E210.4"),sQuery(id+"F7.wireOp",EDGE,"E210.5")])],"isStart":false});
            var sketch = newSketch(context, id + "F9", { "sketchPlane" : qUnion([Q0])});
            skLineSegment(sketch, "E211.0", {"start": v(-1012.76, 126.28) * mm, "end": v(-962.19, -123.72) * mm});
            skLineSegment(sketch, "E211.1", {"start": v(-942.35, -21.84) * mm, "end": v(-973.61, 126.28) * mm});
            skLineSegment(sketch, "E211.2", {"start": v(-973.61, 126.28) * mm, "end": v(-1012.76, 126.28) * mm});
            skLineSegment(sketch, "E211.3", {"start": v(-912.48, 126.28) * mm, "end": v(-942.35, -21.84) * mm});
            skLineSegment(sketch, "E211.4", {"start": v(-871.93, 126.28) * mm, "end": v(-912.48, 126.28) * mm});
            skLineSegment(sketch, "E211.5", {"start": v(-892.27, 28.86) * mm, "end": v(-871.93, 126.28) * mm});
            skLineSegment(sketch, "E211.6", {"start": v(-924.13, -123.75) * mm, "end": v(-892.27, 28.86) * mm});
            skLineSegment(sketch, "E211.7", {"start": v(-962.19, -123.72) * mm, "end": v(-924.13, -123.75) * mm});
            skSolve(sketch);
        }
        {
            var Q0;
            Q0=makeQuery(id+"F9.imprint","IMPRINT",FACE,{"disambiguationData":[TD([[makeQuery(id+"F9.imprint","IMPRINT",EDGE,{"derivedFrom":makeQuery(id+"F8.opExtrude","CAP_EDGE",EDGE,{"disambiguationData":[OSD([sQuery(id+"F7.wireOp",EDGE,"E208.0")])],"isStart":false})}),-1.0]])]});
            var Q1;
            Q1=makeQuery(id+"F9.imprint","IMPRINT",FACE,{"disambiguationData":[TD([[makeQuery(id+"F9.imprint","IMPRINT",EDGE,{"derivedFrom":makeQuery(id+"F8.opExtrude","CAP_EDGE",EDGE,{"disambiguationData":[OSD([sQuery(id+"F7.wireOp",EDGE,"E209.0")])],"isStart":false})}),-1.0]])]});
            var Q2;
            Q2=makeQuery(id+"F9.imprint","IMPRINT",FACE,{"disambiguationData":[TD([[makeQuery(id+"F9.imprint","IMPRINT",EDGE,{"derivedFrom":makeQuery(id+"F8.opExtrude","CAP_EDGE",EDGE,{"disambiguationData":[OSD([sQuery(id+"F7.wireOp",EDGE,"E210.0")])],"isStart":false})}),-1.0]])]});
            var Q3;
            Q3=makeQuery(id+"F9.imprint","IMPRINT",FACE,{"disambiguationData":[TD([[makeQuery(id+"F9.imprint","IMPRINT",EDGE,{"derivedFrom":sQuery(id+"F9.wireOp",EDGE,"E211.0")}),1.0]])]});
            extrude(context, id + "F10", {"entities" : qUnion([Q0, Q1, Q2, Q3]), "depth" : getVariable(context, 'spessore_materiale')});
        }
    });
